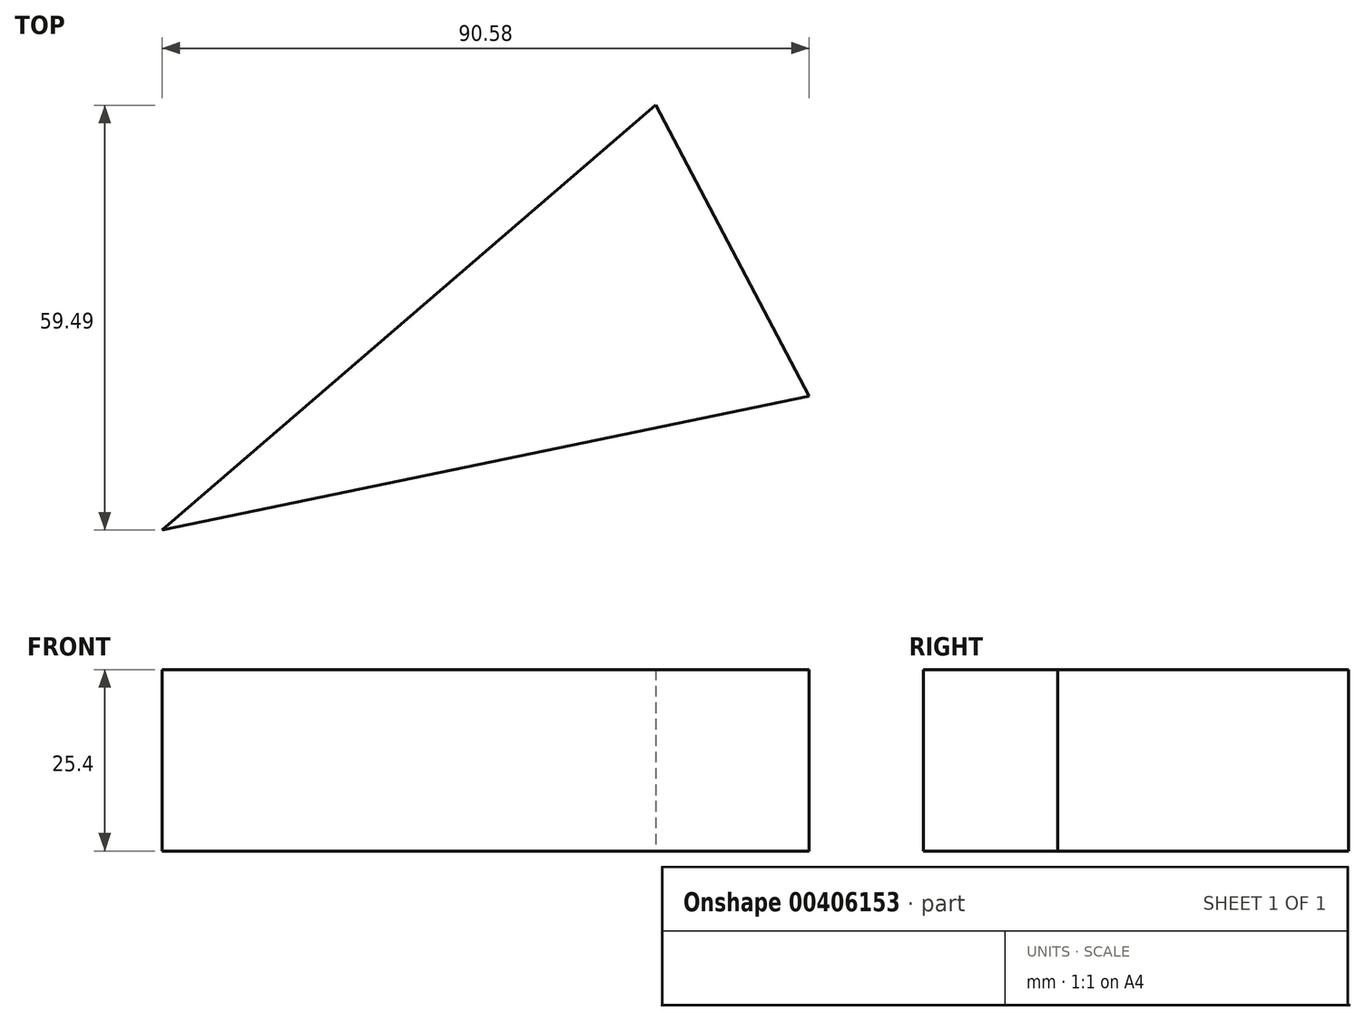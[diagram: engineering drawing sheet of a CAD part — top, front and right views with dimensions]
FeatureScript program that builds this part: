
annotation { "Feature Type Name" : "Feature", "Feature Type Description" : "" }
export const myFeature = defineFeature(function(context is Context, id is Id, definition is map)
    precondition{}
    {
        {
            var Q0;
            Q0=qCreatedBy(makeId("Top.planeOp"),FACE);
            var sketch = newSketch(context, id + "F0", { "sketchPlane" : qUnion([Q0])});
            skLineSegment(sketch, "E0", {"start": v(-48.92, 0) * mm, "end": v(20.2, 59.5) * mm});
            skLineSegment(sketch, "E1", {"start": v(20.2, 59.5) * mm, "end": v(41.66, 18.78) * mm});
            skLineSegment(sketch, "E2", {"start": v(41.66, 18.78) * mm, "end": v(-48.92, 0) * mm});
            skSolve(sketch);
        }
        {
            var Q0;
            Q0=makeQuery(id+"F0.imprint","IMPRINT",FACE,{"disambiguationData":[TD([[makeQuery(id+"F0.imprint","IMPRINT",EDGE,{"derivedFrom":sQuery(id+"F0.wireOp",EDGE,"E0")}),-1.0]])]});
            extrude(context, id + "F1", {"entities" : qUnion([Q0]), "depth" : 25.4 * mm});
        }
    });
